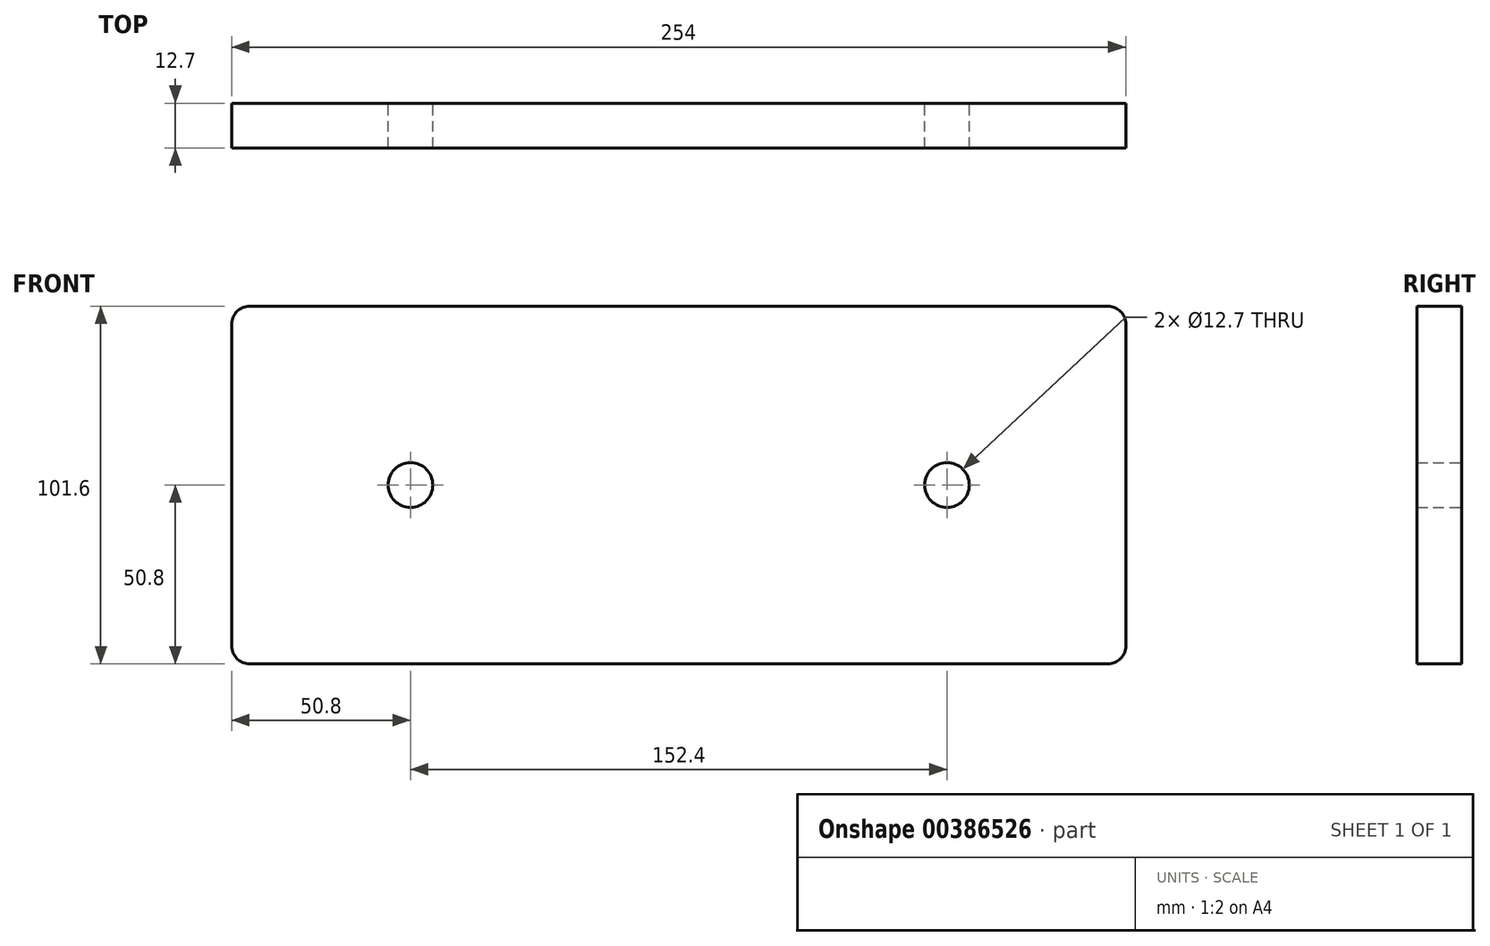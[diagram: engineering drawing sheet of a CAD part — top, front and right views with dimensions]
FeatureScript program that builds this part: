
annotation { "Feature Type Name" : "Feature", "Feature Type Description" : "" }
export const myFeature = defineFeature(function(context is Context, id is Id, definition is map)
    precondition{}
    {
        {
            var Q0;
            Q0=qCreatedBy(makeId("Front.planeOp"),FACE);
            var sketch = newSketch(context, id + "F0", { "sketchPlane" : qUnion([Q0])});
            skLineSegment(sketch, "E0.bottom", {"start": v(0, 0) * mm, "end": v(-254, 0) * mm});
            skLineSegment(sketch, "E0.top", {"start": v(0, 101.6) * mm, "end": v(-254, 101.6) * mm});
            skLineSegment(sketch, "E0.left", {"start": v(0, 0) * mm, "end": v(0, 101.6) * mm});
            skLineSegment(sketch, "E0.right", {"start": v(-254, 0) * mm, "end": v(-254, 101.6) * mm});
            skCircle(sketch, "E1", {"center": v(-203.2, 50.8) * mm, "radius": 6.35 * mm});
            skCircle(sketch, "E2", {"center": v(-50.8, 50.8) * mm, "radius": 6.35 * mm});
            skSolve(sketch);
        }
        {
            var Q0;
            Q0=makeQuery(id+"F0.imprint","IMPRINT",FACE,{"disambiguationData":[TD([[makeQuery(id+"F0.imprint","IMPRINT",EDGE,{"derivedFrom":sQuery(id+"F0.wireOp",EDGE,"E0.bottom")}),-1.0]])]});
            extrude(context, id + "F1", {"entities" : qUnion([Q0]), "depth" : 12.7 * mm});
        }
        {
            var Q0;
            Q0=makeQuery(id+"F1.opExtrude","SWEPT_EDGE",EDGE,{"disambiguationData":[OSD([sQuery(id+"F0.wireOp",EDGE,"E0.top"),sQuery(id+"F0.wireOp",EDGE,"E0.right")])]});
            var Q1;
            Q1=makeQuery(id+"F1.opExtrude","SWEPT_EDGE",EDGE,{"disambiguationData":[OSD([sQuery(id+"F0.wireOp",EDGE,"E0.top"),sQuery(id+"F0.wireOp",EDGE,"E0.left")])]});
            var Q2;
            Q2=makeQuery(id+"F1.opExtrude","SWEPT_EDGE",EDGE,{"disambiguationData":[OSD([sQuery(id+"F0.wireOp",EDGE,"E0.bottom"),sQuery(id+"F0.wireOp",EDGE,"E0.left")])]});
            var Q3;
            Q3=makeQuery(id+"F1.opExtrude","SWEPT_EDGE",EDGE,{"disambiguationData":[OSD([sQuery(id+"F0.wireOp",EDGE,"E0.bottom"),sQuery(id+"F0.wireOp",EDGE,"E0.right")])]});
            fillet(context, id + "F2", {"entities" : qUnion([Q0, Q1, Q2, Q3]), "radius" : 5.08 * mm, "tangentPropagation" : true, "allowEdgeOverflow" : false});
        }
    });
